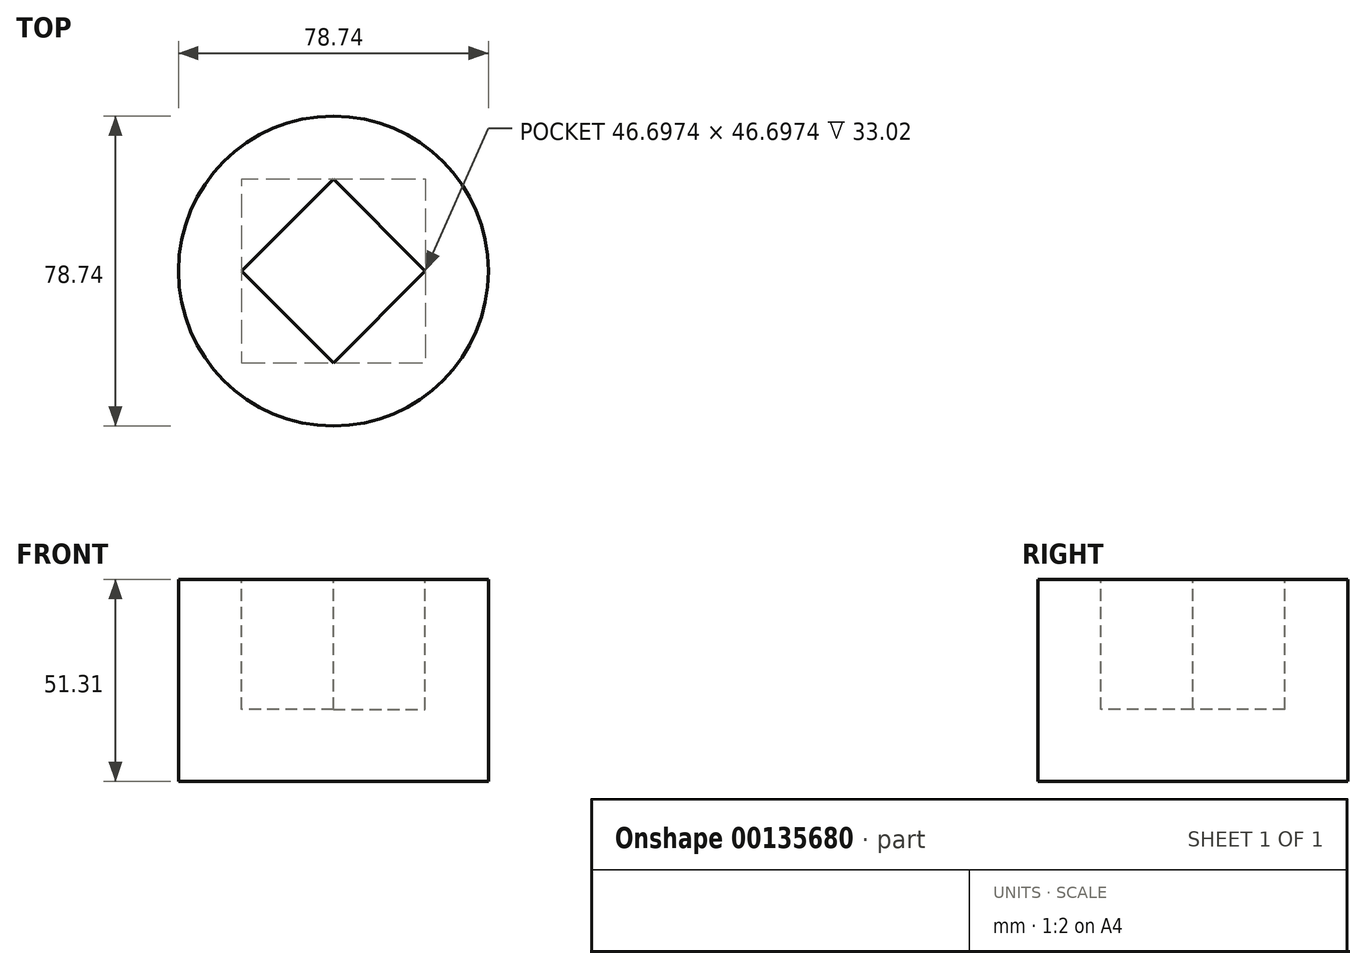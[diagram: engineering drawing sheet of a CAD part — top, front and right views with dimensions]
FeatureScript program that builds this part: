
annotation { "Feature Type Name" : "Feature", "Feature Type Description" : "" }
export const myFeature = defineFeature(function(context is Context, id is Id, definition is map)
    precondition{}
    {
        {
            var Q0;
            Q0=qCreatedBy(makeId("Top.planeOp"),FACE);
            var sketch = newSketch(context, id + "F0", { "sketchPlane" : qUnion([Q0])});
            skCircle(sketch, "E0", {"center": v(0, 0) * mm, "radius": 39.37 * mm});
            skSolve(sketch);
        }
        {
            var Q0;
            Q0=qSketchRegion(id+"F0",true);
            extrude(context, id + "F1", {"entities" : qUnion([Q0]), "oppositeDirection" : true, "depth" : 0.5 * mm});
        }
        {
            var Q0;
            Q0=qCreatedBy(makeId("Top.planeOp"),FACE);
            var sketch = newSketch(context, id + "F2", { "sketchPlane" : qUnion([Q0])});
            skCircle(sketch, "E1", {"center": v(0, 0) * mm, "radius": 39.37 * mm});
            skSolve(sketch);
        }
        {
            var Q0;
            Q0=qSketchRegion(id+"F2",true);
            extrude(context, id + "F3", {"entities" : qUnion([Q0]), "operationType" : NewBodyOperationType.ADD, "depth" : 50.8 * mm});
        }
        {
            var Q0;
            Q0=makeQuery(id+"F3.opExtrude","CAP_FACE",FACE,{"disambiguationData":[OSD([sQuery(id+"F2.wireOp",EDGE,"E1")])],"isStart":false});
            var sketch = newSketch(context, id + "F4", { "sketchPlane" : qUnion([Q0])});
            skLineSegment(sketch, "E2.bottom", {"start": v(0, 23.35) * mm, "end": v(-23.35, 0) * mm});
            skLineSegment(sketch, "E2.top", {"start": v(23.35, 0) * mm, "end": v(0, -23.35) * mm});
            skLineSegment(sketch, "E2.left", {"start": v(0, 23.35) * mm, "end": v(23.35, 0) * mm});
            skLineSegment(sketch, "E2.right", {"start": v(-23.35, 0) * mm, "end": v(0, -23.35) * mm});
            skPoint(sketch, "E2.middle", {"position": v(0, 0) * mm});
            skSolve(sketch);
        }
        {
            var Q0;
            Q0=qSketchRegion(id+"F4",true);
            extrude(context, id + "F5", {"entities" : qUnion([Q0]), "operationType" : NewBodyOperationType.REMOVE, "oppositeDirection" : true, "depth" : 33.02 * mm});
        }
    });
